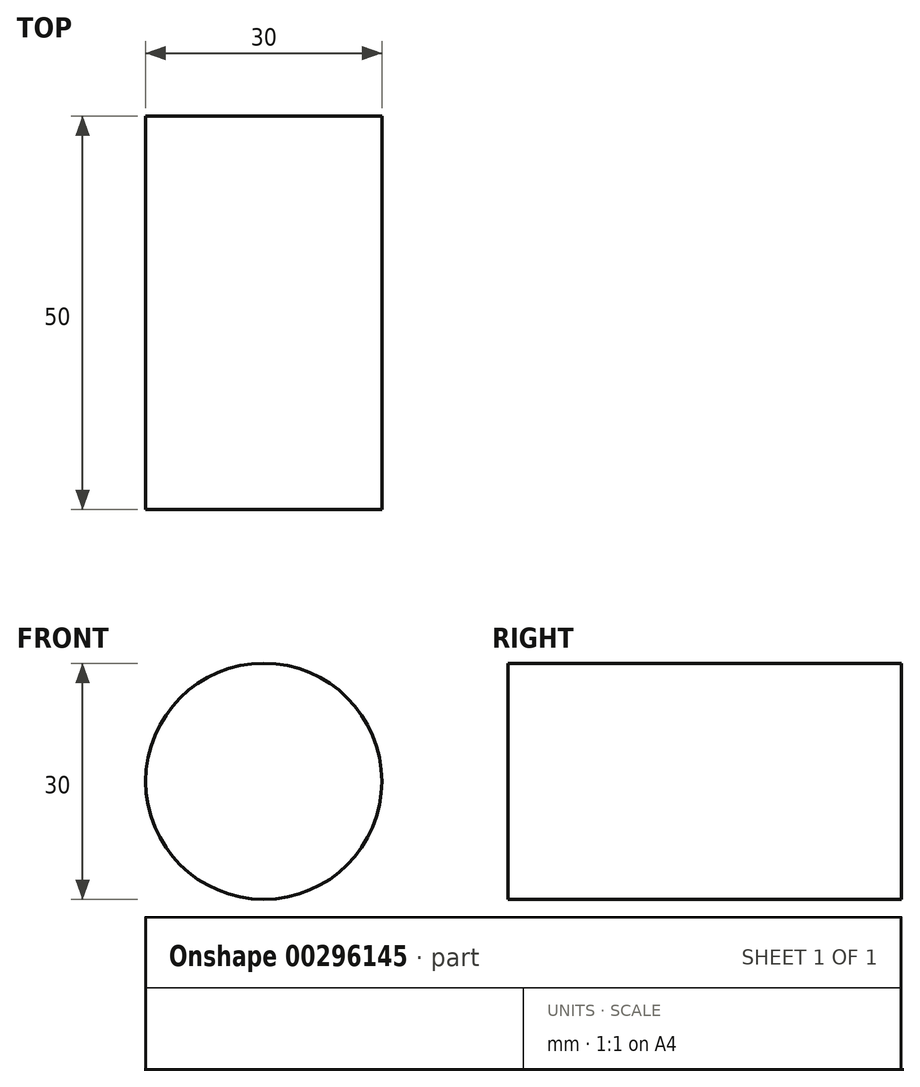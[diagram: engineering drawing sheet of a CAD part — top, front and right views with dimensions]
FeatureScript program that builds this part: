
annotation { "Feature Type Name" : "Feature", "Feature Type Description" : "" }
export const myFeature = defineFeature(function(context is Context, id is Id, definition is map)
    precondition{}
    {
        {
            var Q0;
            Q0=qCreatedBy(makeId("Front.planeOp"),FACE);
            var sketch = newSketch(context, id + "F0", { "sketchPlane" : qUnion([Q0])});
            skCircle(sketch, "E0", {"center": v(0, 0) * mm, "radius": 15 * mm});
            skSolve(sketch);
        }
        {
            var Q0;
            Q0=makeQuery(id+"F0.imprint","IMPRINT",FACE,{"disambiguationData":[TD([[makeQuery(id+"F0.imprint","IMPRINT",EDGE,{"derivedFrom":sQuery(id+"F0.wireOp",EDGE,"E0")}),1.0]])]});
            extrude(context, id + "F1", {"entities" : qUnion([Q0]), "oppositeDirection" : true, "depth" : 50 * mm});
        }
    });
